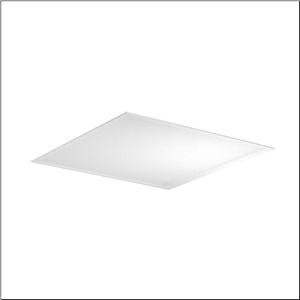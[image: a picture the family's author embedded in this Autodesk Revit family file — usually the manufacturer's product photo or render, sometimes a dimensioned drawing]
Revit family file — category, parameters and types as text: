
# Revit family: apollon_r__21_square_51mq12wd2114_45b2
name_source: partatom
category: Lighting Fixtures
units: mm (PartAtom-declared; Revit-internal decimal feet)

## family parameters
Cut with Voids When Loaded = No
Host = Face
Light Source = No
Part Type = Normal
Room Calculation Point = No
Round Connector Dimension = Use Diameter
Shared = No

## types (1)
- Apollon® 21 square (1 x LED, 4100 lm, 24.7 W, 4000K)
    Apparent Load = 25 VA
    CIE Flux Codes = 60 87 97 100 100
    Color Rendering = 90
    Color Temperature = 4000K
    Default Elevation = 1800 mm
    Description = Apollon® 21 square, office luminaire, primary optical cover: micro prismatic cover, of PMMA, CAT 2 (L<= 3000cd/m²), light emission: direct distribution, primary light characteristic: symmetric, installation type: lay-in mounting, LED, rated luminous flux: 4.100lm, luminous efficacy: 166lm/W, light colour: 940, colour temperature: 4000K, with terminal, 5-pole, mains connection: 220..240V, AC/DC, 0/50..60Hz, rated input power: 24.7W, housing, of aluminium, coated, traffic white (RAL 9016), module: M600, length: 595mm, width: 595mm, height: 30mm, housing upper side, of sheet steel, galvanised, protection rating (complete): IP20, protection rating (lamp compartment, on room side): IP50, insulation class (complete): insulation class II (safety insulation), certification: CE, ENEC, impact resistance: IK03, permissible operating ambient temperature: -20..+45°C, permissible storage temperature: -40..+80°C, packaging unit: 1 piece
    Height = 0 mm  [stored 0 ft]
    Lamp = 1 x LED
    Lamp Light Flux = 4100 lm
    Lamp Power = 24.7 W
    Lamp count = 1
    Length = 595 mm
    Luminous efficacy = 166 lm/W
    Manufacturer = Siteco
    ModVariant = No
    Model = 51MQ12WD2114
    Mounting Place = Ceiling
    Mounting Type = Recessed
    Number of Poles = 1
    OnlyDefault = Yes
    Power Factor = 1
    Product Name = Apollon® 21 square
    Product group = office luminaire | ceiling recessed
    ProductGroupID = 401
    Protection Class = Protection class II
    Protection Degree = IP 20
    RLX_Detail_Level = 1
    RLX_Emergency_Light_Flux = 0 lm
    RLX_Emergency_Type = 0
    RLX_Emergency_Type_DB = No
    RlxData = <blob elided: 12497 chars, md5=e9e67071>
    Socket = socket
    Standby Power = 0 W
    System Light Flux = 4100 lm
    System Power = 25 W
    Type Comments = Product without accessories
    Type Image = l_1291049.jpg
    URL = http://relux.com
    VarID = ---
    Voltage = 0 V
    Weight = 0.00 kg
    Width = 595 mm

note: [stored X ft] marks values corroborated as IEEE doubles in the binary element streams (Revit-internal decimal feet)

## geometry (parser evidence)
native form markers: Sweep x10
no freeform markers — native parametric forms only
